# Revit family: LEGRAND_PRISES_NON_VERROUILLEES_ENCASTREES_IP66_230
name_source: partatom
category: Installations électriques
revit_build: Autodesk Revit 2018 (Build: 20170223_1515(x64)
units: mm (PartAtom-declared; Revit-internal decimal feet)

## family parameters
Conserver l'orientation des annotations = Non
Cote de connecteur circulaire = Utiliser le diamètre
Couper avec des vides une fois chargée = Non
Hôte = Face
Partagée = Non
Point de calcul de pièce = Non
Type d'élément = Normal

## types (9) — shared parameters
Conditions Générale d'Utilisation = https://export.legrand.com
Couleur caractéristique = bleu
Description = Prise au standard international pour montage encastré ou saillie avec accessoire permet la connexion d'appareils de puissance
Elévation par défaut = 1000 mm  [stored 3.28084 ft]
Fabricant = Legrand
Température maximale d'installation = 40°C
Température maximum d'utilisation = 100°C
Température minimum d'installation = -20°C
Température minimum d'utilisation = -50°C
Tension V = 230 V  50/60 Hz  bleu
classe de protection IP = IP66/67-55
installation Encastrée E ou Saillie S = encastré et saillie
matériau du boitier = plastique
résistance aux chocs IK = 09
sans halogène = Non
type de raccordement = bornes à vis

## per-type parameters (varying)
| type | Dia bouchon | Intensité A | Modèle | Nombre de pôles | Position de la Terre h | RAY BOUCHON | Ray | Standard CEI ou NFC | dIA | entraxe de fixation horizontal mm | entraxe de fixation vertical mm | h1 | hauteur mm | largeur mm | profondeur d'encastrement mm | profondeur mm |
| Socle tableau Hypra   IP66/67-55   16 A   200/250 V   2P+T   plast | 68 mm | 16 A | 051126 | 3 | 6 | 34 mm | 21 mm  [stored 0.0688976 ft] | CEI | 42 mm | 52 mm | 60 mm | 43 mm | 72 mm | 64 mm | 40 mm | 85 mm |
| Socle tableau Hypra   IP66/67-55   16 A   200/250 V   3P+T   plast | 79 mm | 16 A | 051127 | 6 | 6 | 40 mm | 24 mm | CEI | 49 mm | 60 mm | 70 mm | 50 mm | 84 mm | 74 mm | 41 mm | 89 mm  [stored 0.291995 ft] |
| Socle tableau entraxe unifié Hypra  IP66/67-55  16 A   200/250 V   2P+T   plast | 84 mm | 16 A | 051146 | 3 | 6 | 42 mm | 26 mm | CEI | 52 mm | 70 mm | 70 mm | 50 mm | 84 mm | 84 mm | 42 mm | 81 mm |
| Socle tableau entraxe unifié Hypra  IP66/67-55  16 A   200/250 V   3P+T   plast | 84 mm | 16 A | 051147 | 4 | 9 | 42 mm | 26 mm | CEI | 52 mm | 70 mm | 70 mm | 50 mm | 84 mm | 84 mm | 43 mm | 84 mm |
| Socle tableau entraxe unifié Hypra  IP66/67-55  32 A   200 250 V   2P+T   plast | 89 mm  [stored 0.291995 ft] | 32 A | 053046 | 3 | 6 | 45 mm | 27 mm | CEI | 55 mm | 70 mm | 70 mm | 56 mm | 94 mm | 84 mm | 54 mm | 104 mm |
| Socle tableau entraxe unifié Hypra  IP66/67-55  32 A   230 V   3P+T   plast | 89 mm  [stored 0.291995 ft] | 32 A | 053047 | 4 | 9 | 45 mm | 27 mm | CEI | 55 mm | 70 mm | 70 mm | 56 mm | 94 mm | 84 mm | 54 mm | 104 mm |
| Socle tableau Hypra   IP66/67-55  16 A   250 V   2P+T   brochage domestique   plast | 67 mm | 16 A | 053911 | 3 | 6 | 34 mm | 21 mm  [stored 0.0688976 ft] | NFC | 41 mm | 55 mm | 55 mm | 40 mm | 67 mm | 67 mm | 15 mm | 63 mm  [stored 0.206693 ft] |
| Socle de tableau Hypra  IP66/67-55   63A   200 250 V   2P+T   plast | 106 mm | 63 A | 059326 | 3 | 6 | 53 mm  [stored 0.173885 ft] | 33 mm | CEI | 65 mm | 77 mm | 85 mm | 64 mm | 106 mm | 106 mm | 85 mm | 164 mm |
| Socle tableau Hypra  IP66/67-55  63 A    230 V   3P+T   plast | 106 mm | 63 A | 059327 | 4 | 9 | 53 mm  [stored 0.173885 ft] | 33 mm | CEI | 65 mm | 77 mm | 85 mm | 64 mm | 106 mm | 106 mm | 85 mm | 164 mm |

note: [stored X ft] marks values corroborated as IEEE doubles in the binary element streams (Revit-internal decimal feet)
